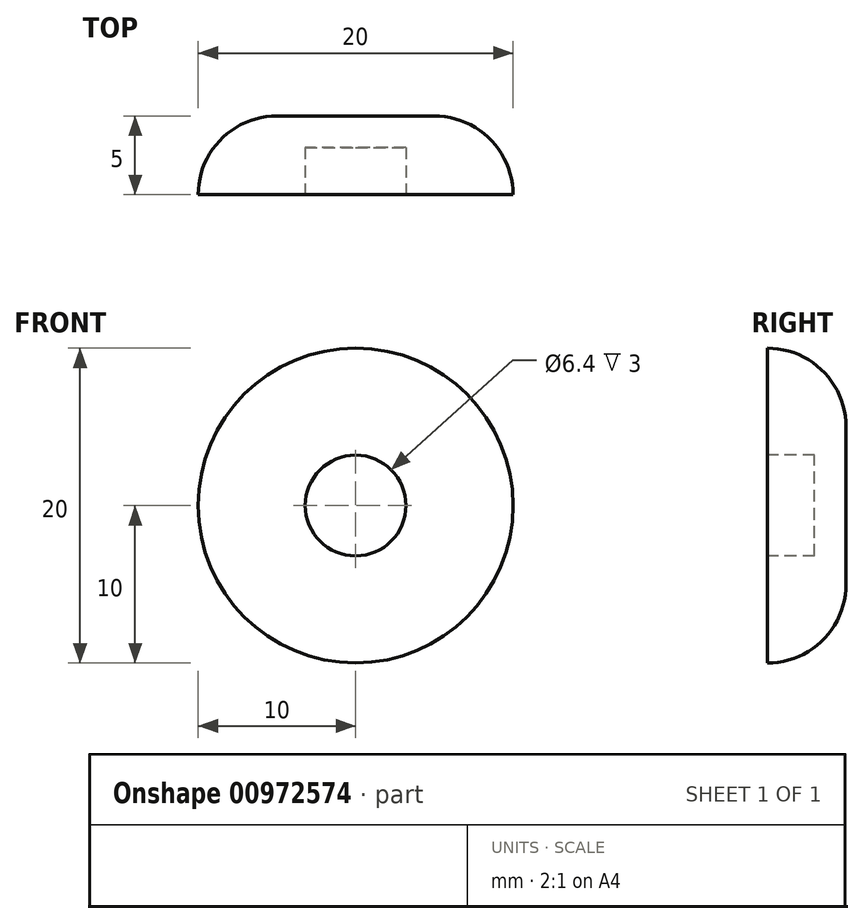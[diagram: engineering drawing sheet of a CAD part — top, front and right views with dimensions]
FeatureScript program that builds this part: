
annotation { "Feature Type Name" : "Feature", "Feature Type Description" : "" }
export const myFeature = defineFeature(function(context is Context, id is Id, definition is map)
    precondition{}
    {
        {
            var Q0;
            Q0=qCreatedBy(makeId("Front.planeOp"),FACE);
            var sketch = newSketch(context, id + "F0", { "sketchPlane" : qUnion([Q0])});
            skCircle(sketch, "E0", {"center": v(0, 0) * mm, "radius": 10 * mm});
            skSolve(sketch);
        }
        {
            var Q0;
            Q0=makeQuery(id+"F0.imprint","IMPRINT",FACE,{"disambiguationData":[TD([[makeQuery(id+"F0.imprint","IMPRINT",EDGE,{"derivedFrom":sQuery(id+"F0.wireOp",EDGE,"E0")}),1.0]])]});
            extrude(context, id + "F1", {"entities" : qUnion([Q0]), "oppositeDirection" : true, "depth" : 5 * mm, "offsetDistance" : 25 * mm});
        }
        {
            var Q0;
            Q0=makeQuery(id+"F1.opExtrude","CAP_EDGE",EDGE,{"disambiguationData":[OSD([sQuery(id+"F0.wireOp",EDGE,"E0")])],"isStart":false});
            fillet(context, id + "F2", {"entities" : qUnion([Q0]), "radius" : 5 * mm, "tangentPropagation" : true, "allowEdgeOverflow" : false});
        }
        {
            var Q0;
            Q0=qCreatedBy(makeId("Front.planeOp"),FACE);
            var sketch = newSketch(context, id + "F3", { "sketchPlane" : qUnion([Q0])});
            skCircle(sketch, "E1", {"center": v(0, 0) * mm, "radius": 3.2 * mm});
            skSolve(sketch);
        }
        {
            var Q0;
            Q0 = qSketchRegion(id + "F3", true);
            extrude(context, id + "F4", {"entities" : qUnion([Q0]), "operationType" : NewBodyOperationType.REMOVE, "oppositeDirection" : true, "depth" : 3 * mm, "offsetDistance" : 25 * mm});
        }
    });
